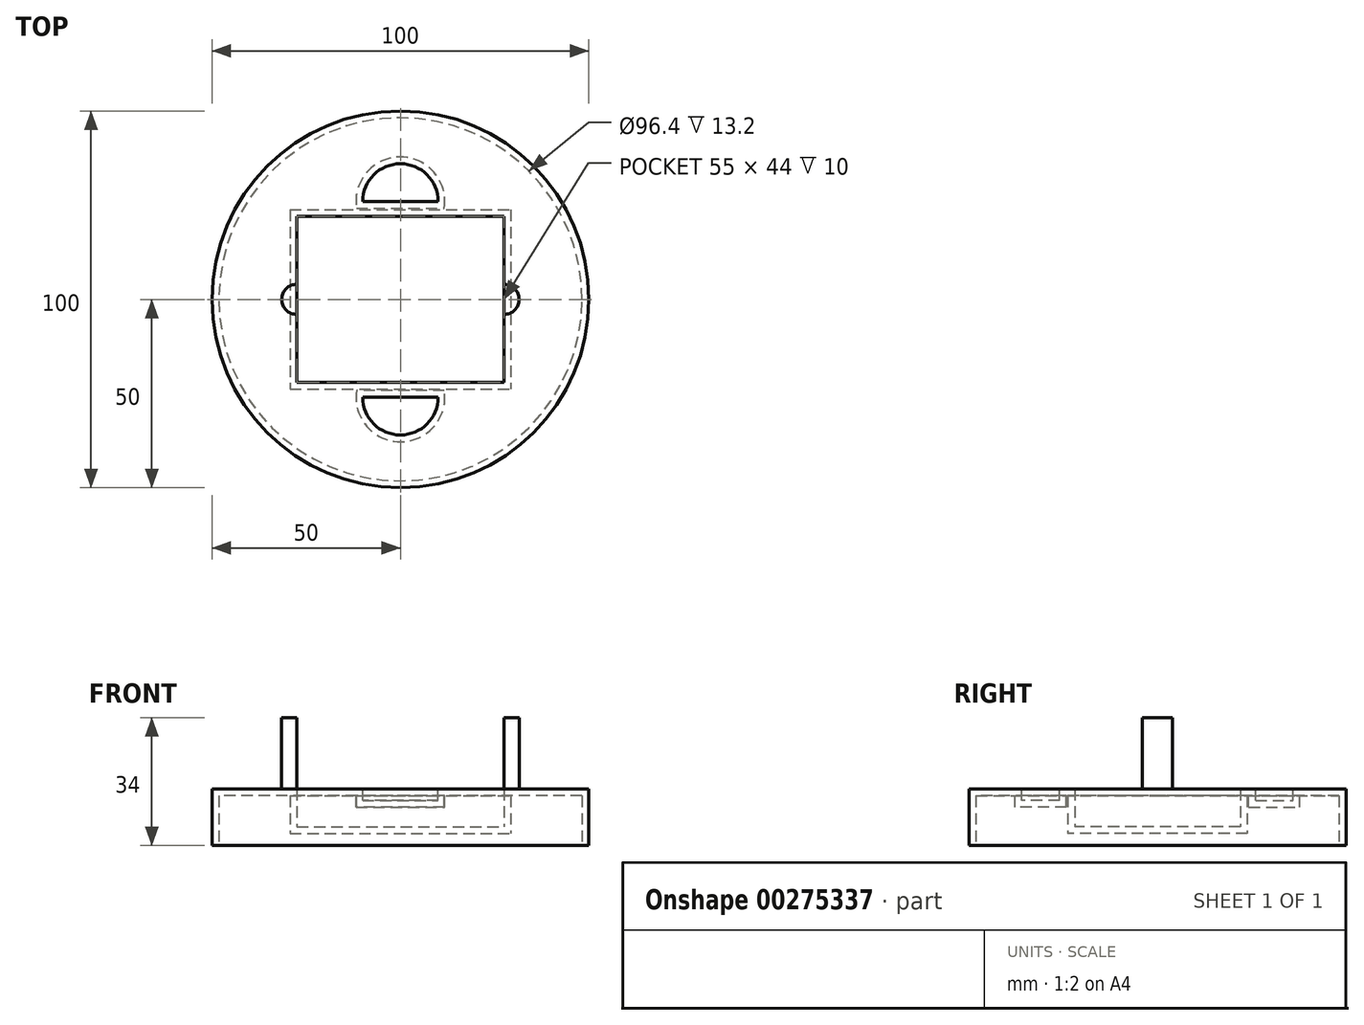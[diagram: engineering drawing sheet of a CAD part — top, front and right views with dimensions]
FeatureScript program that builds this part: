
annotation { "Feature Type Name" : "Feature", "Feature Type Description" : "" }
export const myFeature = defineFeature(function(context is Context, id is Id, definition is map)
    precondition{}
    {
        {
            var Q0;
            Q0=qCreatedBy(makeId("Top.planeOp"),FACE);
            var sketch = newSketch(context, id + "F0", { "sketchPlane" : qUnion([Q0])});
            skLineSegment(sketch, "E0.bottom", {"start": v(-27.5, 22) * mm, "end": v(27.5, 22) * mm});
            skLineSegment(sketch, "E0.top", {"start": v(-27.5, -22) * mm, "end": v(27.5, -22) * mm});
            skLineSegment(sketch, "E0.left", {"start": v(-27.5, 22) * mm, "end": v(-27.5, -22) * mm});
            skLineSegment(sketch, "E0.right", {"start": v(27.5, 22) * mm, "end": v(27.5, -22) * mm});
            skPoint(sketch, "E0.middle", {"position": v(0, 0) * mm});
            skCircle(sketch, "E1", {"center": v(0, 0) * mm, "radius": 50 * mm});
            skPoint(sketch, "E2.start.orphan", {"position": v(-27.5, 0) * mm});
            skPoint(sketch, "E3.start.orphan", {"position": v(27.5, 0) * mm});
            skPoint(sketch, "E4.endSnap0", {"position": v(0, 22) * mm});
            skPoint(sketch, "E5.endSnap0", {"position": v(0, -22) * mm});
            skPoint(sketch, "E5.start.orphan", {"position": v(0, -22) * mm});
            skPoint(sketch, "E4.start.orphan", {"position": v(0, 22) * mm});
            skPoint(sketch, "E6.start.orphan", {"position": v(0, 26) * mm});
            skPoint(sketch, "E7.start.orphan", {"position": v(0, -26) * mm});
            skSolve(sketch);
        }
        {
            var Q0;
            Q0=makeQuery(id+"F0.imprint","IMPRINT",FACE,{"disambiguationData":[TD([[makeQuery(id+"F0.imprint","IMPRINT",EDGE,{"derivedFrom":sQuery(id+"F0.wireOp",EDGE,"E0.bottom")}),1.0]])]});
            extrude(context, id + "F1", {"entities" : qUnion([Q0]), "depth" : 15 * mm});
        }
        {
            var Q0;
            Q0=makeQuery(id+"F0.imprint","IMPRINT",FACE,{"disambiguationData":[TD([[makeQuery(id+"F0.imprint","IMPRINT",EDGE,{"derivedFrom":sQuery(id+"F0.wireOp",EDGE,"E0.bottom")}),-1.0]])]});
            extrude(context, id + "F2", {"entities" : qUnion([Q0]), "operationType" : NewBodyOperationType.ADD, "depth" : 5 * mm});
        }
        {
            var Q0;
            Q0=qCreatedBy(makeId("Top.planeOp"),FACE);
            cPlane(context, id + "F3", {"entities" : qUnion([Q0]), "cplaneType" : CPlaneType.OFFSET, "offset" : 15 * mm, "width" : 150 * mm, "height" : 150 * mm});
        }
        {
            var Q0;
            Q0=qCreatedBy(id+"F3.planeOp",FACE);
            var sketch = newSketch(context, id + "F4", { "sketchPlane" : qUnion([Q0])});
            skPoint(sketch, "E8.end.orphan", {"position": v(43.55, 0) * mm});
            skPoint(sketch, "E9.start.orphan", {"position": v(0, 0) * mm});
            skLineSegment(sketch, "E10", {"start": v(0, -26) * mm, "end": v(-5, -26) * mm});
            skLineSegment(sketch, "E11", {"start": v(0, -26) * mm, "end": v(5, -26) * mm});
            skLineSegment(sketch, "E12", {"start": v(0, 26) * mm, "end": v(5, 26) * mm});
            skLineSegment(sketch, "E13", {"start": v(0, 26) * mm, "end": v(-5, 26) * mm});
            skArc(sketch, "E14", {"start": v(10, 26) * mm, "mid": v(0, 36) * mm, "end": v(-10, 26) * mm});
            skArc(sketch, "E15", {"start": v(-10, -26) * mm, "mid": v(0, -36) * mm, "end": v(10, -26) * mm});
            skLineSegment(sketch, "E16", {"start": v(0, 26) * mm, "end": v(10, 26) * mm});
            skLineSegment(sketch, "E17", {"start": v(0, 26) * mm, "end": v(-10, 26) * mm});
            skLineSegment(sketch, "E18", {"start": v(0, -26) * mm, "end": v(-10, -26) * mm});
            skLineSegment(sketch, "E19", {"start": v(0, -26) * mm, "end": v(10, -26) * mm});
            skLineSegment(sketch, "E20", {"start": v(0, 0) * mm, "end": v(27.5, 0) * mm});
            skLineSegment(sketch, "E21", {"start": v(0, 0) * mm, "end": v(-27.5, 0) * mm});
            skArc(sketch, "E22", {"start": v(-27.5, 4) * mm, "mid": v(-31.5, 0) * mm, "end": v(-27.5, -4) * mm});
            skArc(sketch, "E23", {"start": v(27.5, -4) * mm, "mid": v(31.5, 0) * mm, "end": v(27.5, 4) * mm});
            skLineSegment(sketch, "E24", {"start": v(-27.5, 4) * mm, "end": v(-27.5, -4) * mm});
            skLineSegment(sketch, "E25", {"start": v(27.5, 4) * mm, "end": v(27.5, -4) * mm});
            skSolve(sketch);
        }
        {
            var Q0;
            {var subQ4=sQuery(id+"F4.wireOp",EDGE,"E14");Q0=makeQuery(id+"F4.imprint","IMPRINT",FACE,{"disambiguationData":[TD([[makeQuery(id+"F4.imprint","IMPRINT",EDGE,{"derivedFrom":subQ4}),1.0]])]});}
            var Q1;
            {var subQ4=sQuery(id+"F4.wireOp",EDGE,"E15");Q1=makeQuery(id+"F4.imprint","IMPRINT",FACE,{"disambiguationData":[TD([[makeQuery(id+"F4.imprint","IMPRINT",EDGE,{"derivedFrom":subQ4}),1.0]])]});}
            extrude(context, id + "F5", {"entities" : qUnion([Q0, Q1]), "operationType" : NewBodyOperationType.REMOVE, "oppositeDirection" : true, "depth" : 3 * mm});
        }
        {
            var Q0;
            {var subQ0=sQuery(id+"F0.wireOp",EDGE,"E0.right");var subQ1=sQuery(id+"F0.wireOp",EDGE,"E0.left");var subQ2=sQuery(id+"F0.wireOp",EDGE,"E0.top");var subQ3=sQuery(id+"F0.wireOp",EDGE,"E0.bottom");Q0=makeQuery(id+"F2.boolean.opBoolean","MERGE",FACE,{"derivedFrom":[makeQuery(id+"F1.opExtrude","CAP_FACE",FACE,{"disambiguationData":[OSD([subQ3,subQ2,subQ1,subQ0,sQuery(id+"F0.wireOp",EDGE,"E1")])],"isStart":true}),makeQuery(id+"F2.opExtrude","CAP_FACE",FACE,{"disambiguationData":[OSD([subQ3,subQ2,subQ1,subQ0])],"isStart":true})]});}
            shell(context, id + "F6", {"entities" : qUnion([Q0]), "thickness" : 1.8 * mm});
        }
        {
            var Q0;
            {var subQ0=sQuery(id+"F4.wireOp",EDGE,"E22");Q0=makeQuery(id+"F4.imprint","IMPRINT",FACE,{"disambiguationData":[TD([[makeQuery(id+"F4.imprint","IMPRINT",EDGE,{"derivedFrom":subQ0}),1.0]])]});}
            var Q1;
            {var subQ0=sQuery(id+"F4.wireOp",EDGE,"E23");Q1=makeQuery(id+"F4.imprint","IMPRINT",FACE,{"disambiguationData":[TD([[makeQuery(id+"F4.imprint","IMPRINT",EDGE,{"derivedFrom":subQ0}),1.0]])]});}
            extrude(context, id + "F7", {"entities" : qUnion([Q0, Q1]), "operationType" : NewBodyOperationType.ADD, "depth" : 19 * mm});
        }
    });
